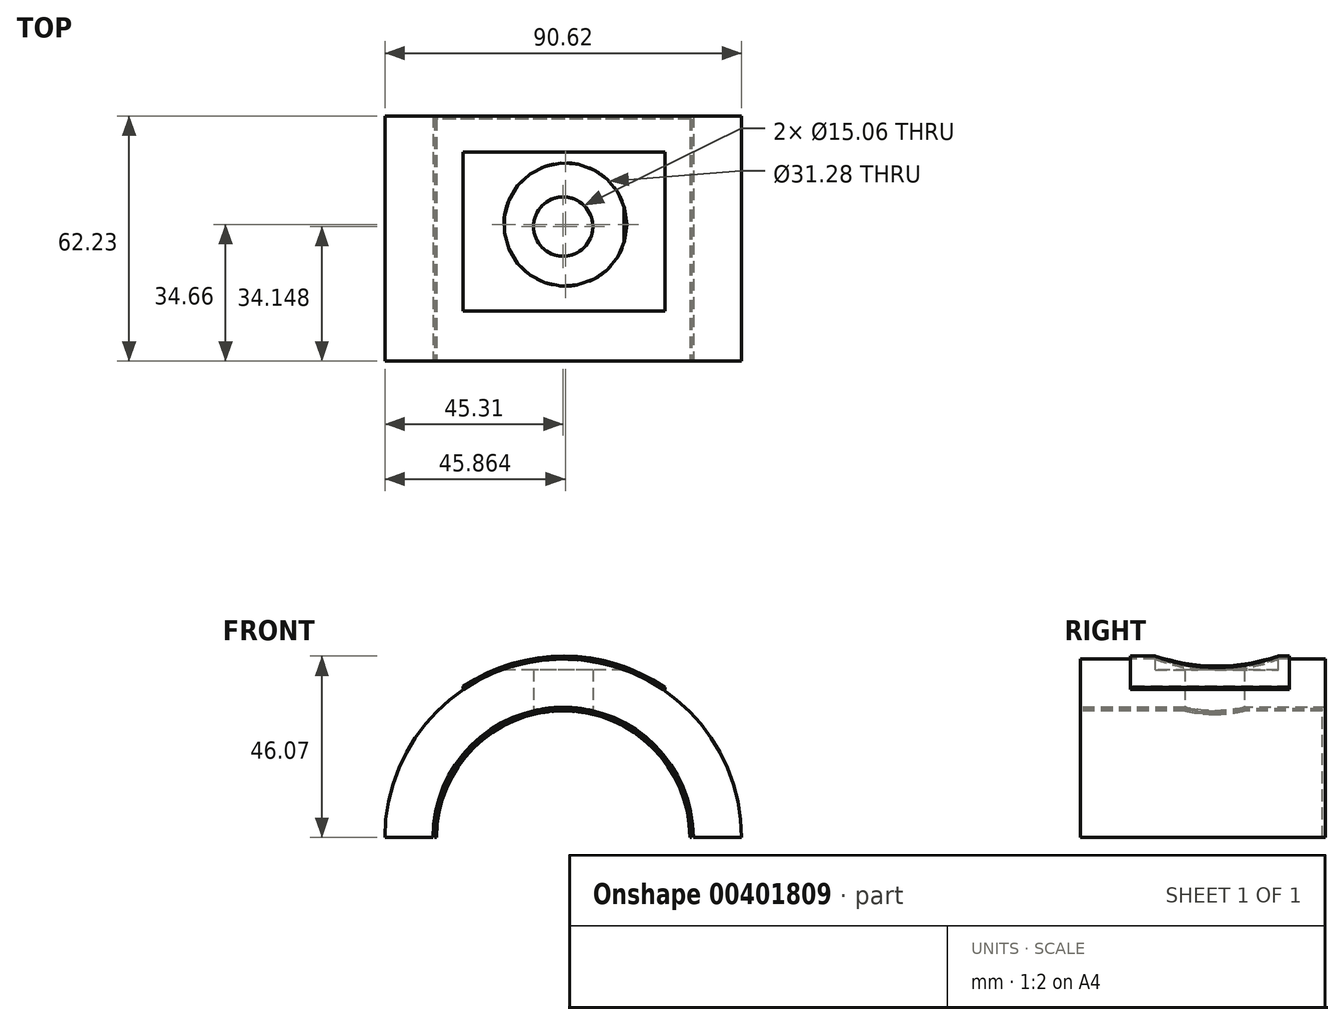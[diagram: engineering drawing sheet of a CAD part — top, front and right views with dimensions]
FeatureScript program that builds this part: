
annotation { "Feature Type Name" : "Feature", "Feature Type Description" : "" }
export const myFeature = defineFeature(function(context is Context, id is Id, definition is map)
    precondition{}
    {
        {
            var Q0;
            Q0=qCreatedBy(makeId("Front.planeOp"),FACE);
            var sketch = newSketch(context, id + "F0", { "sketchPlane" : qUnion([Q0])});
            skArc(sketch, "E0", {"start": v(45.31, 0) * mm, "mid": v(0, 45.31) * mm, "end": v(-45.31, 0) * mm});
            skArc(sketch, "E1", {"start": v(33.07, 0) * mm, "mid": v(0, 33.07) * mm, "end": v(-33.07, 0) * mm});
            skLineSegment(sketch, "E2", {"start": v(-45.31, 0) * mm, "end": v(-33.07, 0) * mm});
            skLineSegment(sketch, "E3.trimOffspring", {"start": v(33.07, 0) * mm, "end": v(45.31, 0) * mm});
            skPoint(sketch, "E4.orphan", {"position": v(-51.72, 0) * mm});
            skLineSegment(sketch, "E5.trimOffspring", {"start": v(-33.07, 0) * mm, "end": v(-45.31, 0) * mm});
            skSolve(sketch);
        }
        {
            var Q0;
            Q0=makeQuery(id+"F0.imprint","IMPRINT",FACE,{"disambiguationData":[TD([[makeQuery(id+"F0.imprint","IMPRINT",EDGE,{"derivedFrom":sQuery(id+"F0.wireOp",EDGE,"E0")}),1.0]])]});
            extrude(context, id + "F1", {"entities" : qUnion([Q0]), "oppositeDirection" : true, "depth" : 62.23 * mm});
        }
        {
            var Q0;
            Q0=qCreatedBy(makeId("Top.planeOp"),FACE);
            var sketch = newSketch(context, id + "F2", { "sketchPlane" : qUnion([Q0])});
            skCircle(sketch, "E6", {"center": v(0, 34.15) * mm, "radius": 7.53 * mm});
            skSolve(sketch);
        }
        {
            var Q0;
            Q0=qCreatedBy(makeId("Front.planeOp"),FACE);
            cPlane(context, id + "F3", {"entities" : qUnion([Q0]), "cplaneType" : CPlaneType.OFFSET, "offset" : 12.7 * mm, "oppositeDirection" : true, "width" : 152.4 * mm, "height" : 152.4 * mm});
        }
        {
            var Q0;
            Q0=qCreatedBy(id+"F3.planeOp",FACE);
            var sketch = newSketch(context, id + "F4", { "sketchPlane" : qUnion([Q0])});
            skLineSegment(sketch, "E7", {"start": v(-33.07, 0) * mm, "end": v(-55.97, 0) * mm});
            skLineSegment(sketch, "E8", {"start": v(-33.07, 0) * mm, "end": v(-33.07, 0) * mm});
            skLineSegment(sketch, "E9", {"start": v(1.5, 0) * mm, "end": v(-33.07, 0) * mm});
            skLineSegment(sketch, "E10", {"start": v(1.5, 0) * mm, "end": v(50.15, 0) * mm});
            skCircle(sketch, "E11", {"center": v(0.05, 0) * mm, "radius": 45.61 * mm});
            skCircle(sketch, "E12", {"center": v(0.05, 0) * mm, "radius": 46.07 * mm});
            skLineSegment(sketch, "E13", {"start": v(0.05, 0) * mm, "end": v(-19.11, 0) * mm});
            skLineSegment(sketch, "E14", {"start": v(0.05, 0) * mm, "end": v(18.74, 0) * mm});
            skLineSegment(sketch, "E15", {"start": v(0.05, 0) * mm, "end": v(-17.82, 0) * mm});
            skLineSegment(sketch, "E16", {"start": v(0.05, 0) * mm, "end": v(-25.4, 0) * mm});
            skLineSegment(sketch, "E17", {"start": v(-25.4, 0) * mm, "end": v(-25.4, 61.91) * mm});
            skLineSegment(sketch, "E18", {"start": v(0.05, 0) * mm, "end": v(25.83, 0) * mm});
            skLineSegment(sketch, "E19", {"start": v(25.83, 0) * mm, "end": v(25.83, 62.26) * mm});
            skSolve(sketch);
        }
        {
            var Q0;
            {var subQ0=sQuery(id+"F4.wireOp",EDGE,"E19");var subQ1=sQuery(id+"F4.wireOp",EDGE,"E11");var subQ2=makeQuery(id+"F4.imprint","INTERSECT",VERTEX,{"derivedFrom":[subQ1,subQ0]});Q0=makeQuery(id+"F4.imprint","IMPRINT",FACE,{"disambiguationData":[TD([[makeQuery(id+"F4.imprint","IMPRINT",EDGE,{"disambiguationData":[TD([[subQ2,-1.0]])],"derivedFrom":subQ1}),-1.0]])]});}
            extrude(context, id + "F5", {"entities" : qUnion([Q0]), "oppositeDirection" : true, "depth" : 40.4 * mm});
        }
        {
            var Q0;
            Q0=qCreatedBy(makeId("Top.planeOp"),FACE);
            cPlane(context, id + "F6", {"entities" : qUnion([Q0]), "cplaneType" : CPlaneType.OFFSET, "offset" : 48.5 * mm, "width" : 152.4 * mm, "height" : 152.4 * mm});
        }
        {
            var Q0;
            Q0=qCreatedBy(id+"F6.planeOp",FACE);
            var sketch = newSketch(context, id + "F7", { "sketchPlane" : qUnion([Q0])});
            skCircle(sketch, "E20", {"center": v(0.55, 34.66) * mm, "radius": 15.64 * mm});
            skSolve(sketch);
        }
        {
            var Q0;
            Q0 = qSketchRegion(id + "F7", true);
            extrude(context, id + "F8", {"entities" : qUnion([Q0]), "operationType" : NewBodyOperationType.REMOVE, "oppositeDirection" : true, "depth" : 5.92 * mm});
        }
        {
            var Q0;
            Q0=qCreatedBy(makeId("Front.planeOp"),FACE);
            var sketch = newSketch(context, id + "F9", { "sketchPlane" : qUnion([Q0])});
            skArc(sketch, "E21", {"start": v(32.17, 0) * mm, "mid": v(0, 32.17) * mm, "end": v(-32.17, 0) * mm});
            skArc(sketch, "E22", {"start": v(32.65, 0) * mm, "mid": v(0, 32.65) * mm, "end": v(-32.65, 0) * mm});
            skLineSegment(sketch, "E23", {"start": v(32.17, 0) * mm, "end": v(32.65, 0) * mm});
            skLineSegment(sketch, "E24", {"start": v(-32.17, 0) * mm, "end": v(-32.65, 0) * mm});
            skSolve(sketch);
        }
        {
            var Q0;
            Q0 = qSketchRegion(id + "F9", true);
            extrude(context, id + "F10", {"entities" : qUnion([Q0]), "oppositeDirection" : true, "depth" : 61.47 * mm});
        }
        {
            var Q0;
            Q0 = qSketchRegion(id + "F2", true);
            extrude(context, id + "F11", {"entities" : qUnion([Q0]), "operationType" : NewBodyOperationType.REMOVE, "depth" : 61.2 * mm});
        }
    });
